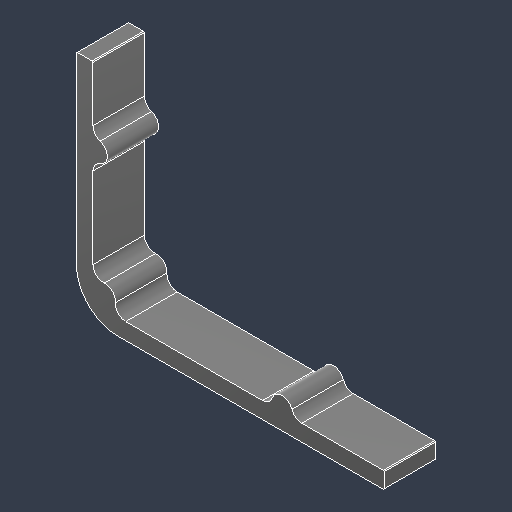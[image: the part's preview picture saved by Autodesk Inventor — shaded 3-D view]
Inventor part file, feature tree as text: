
AUTODESK INVENTOR PART (.ipt)
format: ipt  version: 2023.4 (Build 274418000, 418)  size: 128,000 bytes
history: native  units: mm
features: other x3, sketch x3
ambient origin geometry x8: Origin, YZ Plane, XZ Plane, XY Plane, X Axis, Y Axis, Z Axis, Center Point
bodies: Solid1 (feature_tree)
feature tree (6):
  other  "Corner.ipt"
  other  "Solid1::Corner.ipt"
  other  "TaggingFeature1"
  sketch  "Sketch1"  dims[d0=10.0mm]
  sketch  "Sketch2"
  sketch  "Sketch3"
